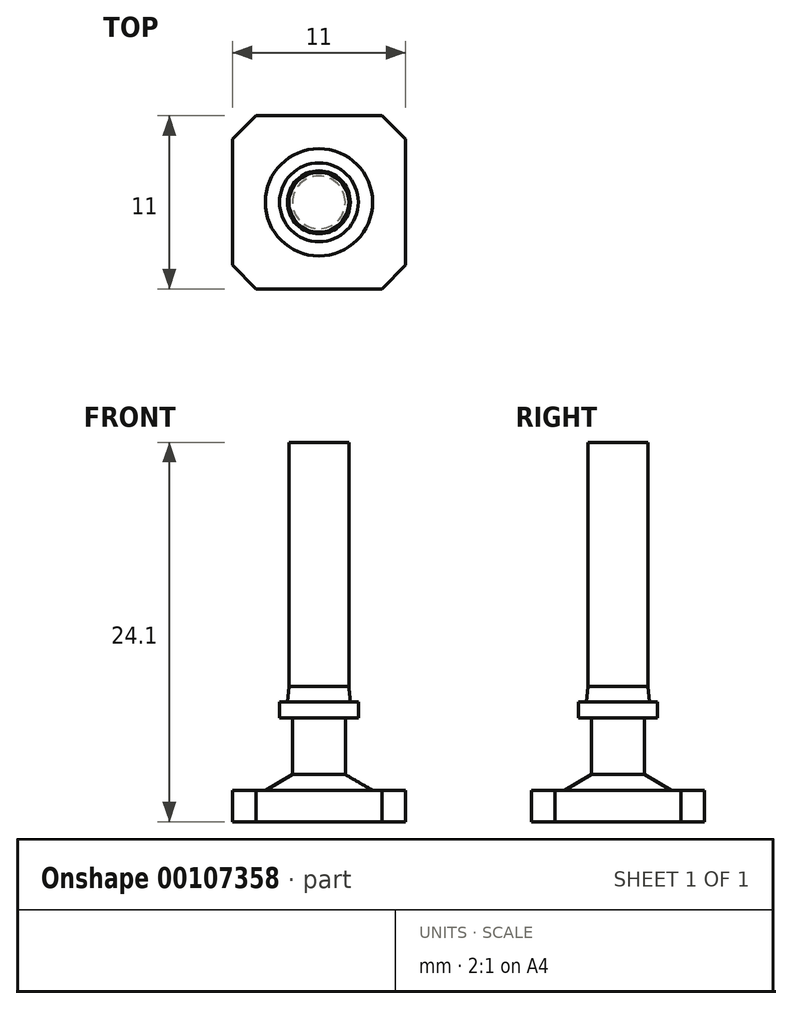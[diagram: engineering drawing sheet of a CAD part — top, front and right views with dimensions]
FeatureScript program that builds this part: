
annotation { "Feature Type Name" : "Feature", "Feature Type Description" : "" }
export const myFeature = defineFeature(function(context is Context, id is Id, definition is map)
    precondition{}
    {
        {
            var Q0;
            Q0=qCreatedBy(makeId("Right.planeOp"),FACE);
            var sketch = newSketch(context, id + "F0", { "sketchPlane" : qUnion([Q0])});
            skLineSegment(sketch, "E0", {"start": v(-3.4, 0) * mm, "end": v(-1.68, 1) * mm});
            skLineSegment(sketch, "E1", {"start": v(-1.68, 1) * mm, "end": v(-1.68, 4.6) * mm});
            skLineSegment(sketch, "E2", {"start": v(-1.68, 4.6) * mm, "end": v(-2.5, 4.6) * mm});
            skLineSegment(sketch, "E3", {"start": v(-2.5, 4.6) * mm, "end": v(-2.5, 5.6) * mm});
            skLineSegment(sketch, "E4", {"start": v(-2.5, 5.6) * mm, "end": v(-2, 5.6) * mm});
            skLineSegment(sketch, "E5", {"start": v(-2, 5.6) * mm, "end": v(-1.9, 6.6) * mm});
            skLineSegment(sketch, "E6", {"start": v(-1.9, 6.6) * mm, "end": v(-1.9, 22.1) * mm});
            skLineSegment(sketch, "E7", {"start": v(-1.9, 22.1) * mm, "end": v(0, 22.1) * mm});
            skLineSegment(sketch, "E8", {"start": v(0, 22.1) * mm, "end": v(0, 0) * mm});
            skLineSegment(sketch, "E9", {"start": v(-3.4, 0) * mm, "end": v(0, 0) * mm});
            skSolve(sketch);
        }
        {
            var Q0;
            Q0=makeQuery(id+"F0.imprint","IMPRINT",FACE,{"disambiguationData":[TD([[makeQuery(id+"F0.imprint","IMPRINT",EDGE,{"derivedFrom":sQuery(id+"F0.wireOp",EDGE,"E0")}),-1.0]])]});
            var Q1;
            Q1=sQuery(id+"F0.wireOp",EDGE,"E8");
            revolve(context, id + "F1", {"entities" : qUnion([Q0]), "axis" : qUnion([Q1]), "revolveType" : RevolveType.FULL});
        }
        {
            var Q0;
            Q0=qCreatedBy(makeId("Top.planeOp"),FACE);
            var sketch = newSketch(context, id + "F2", { "sketchPlane" : qUnion([Q0])});
            skLineSegment(sketch, "E10", {"start": v(-5.5, -5.5) * mm, "end": v(5.5, -5.5) * mm});
            skLineSegment(sketch, "E11", {"start": v(5.5, -5.5) * mm, "end": v(5.5, 5.5) * mm});
            skLineSegment(sketch, "E12", {"start": v(5.5, 5.5) * mm, "end": v(-5.5, 5.5) * mm});
            skLineSegment(sketch, "E13", {"start": v(-5.5, 5.5) * mm, "end": v(-5.5, -5.5) * mm});
            skLineSegment(sketch, "E14", {"start": v(0, -5.5) * mm, "end": v(0, 5.5) * mm, "construction": true});
            skLineSegment(sketch, "E15", {"start": v(-5.5, 0) * mm, "end": v(5.5, 0) * mm, "construction": true});
            skSolve(sketch);
        }
        {
            var Q0;
            Q0=makeQuery(id+"F2.imprint","IMPRINT",FACE,{"disambiguationData":[TD([[makeQuery(id+"F2.imprint","IMPRINT",EDGE,{"derivedFrom":sQuery(id+"F2.wireOp",EDGE,"E10")}),1.0]])]});
            extrude(context, id + "F3", {"entities" : qUnion([Q0]), "operationType" : NewBodyOperationType.ADD, "oppositeDirection" : true, "depth" : 2 * mm});
        }
        {
            var Q0;
            Q0=makeQuery(id+"F3.opExtrude","SWEPT_EDGE",EDGE,{"disambiguationData":[OSD([sQuery(id+"F2.wireOp",EDGE,"E12"),sQuery(id+"F2.wireOp",EDGE,"E13")])]});
            var Q1;
            Q1=makeQuery(id+"F3.opExtrude","SWEPT_EDGE",EDGE,{"disambiguationData":[OSD([sQuery(id+"F2.wireOp",EDGE,"E11"),sQuery(id+"F2.wireOp",EDGE,"E12")])]});
            var Q2;
            Q2=makeQuery(id+"F3.opExtrude","SWEPT_EDGE",EDGE,{"disambiguationData":[OSD([sQuery(id+"F2.wireOp",EDGE,"E10"),sQuery(id+"F2.wireOp",EDGE,"E11")])]});
            var Q3;
            Q3=makeQuery(id+"F3.opExtrude","SWEPT_EDGE",EDGE,{"disambiguationData":[OSD([sQuery(id+"F2.wireOp",EDGE,"E10"),sQuery(id+"F2.wireOp",EDGE,"E13")])]});
            chamfer(context, id + "F4", {"entities" : qUnion([Q0, Q1, Q2, Q3]), "width" : 1.5 * mm, "tangentPropagation" : true});
        }
    });
